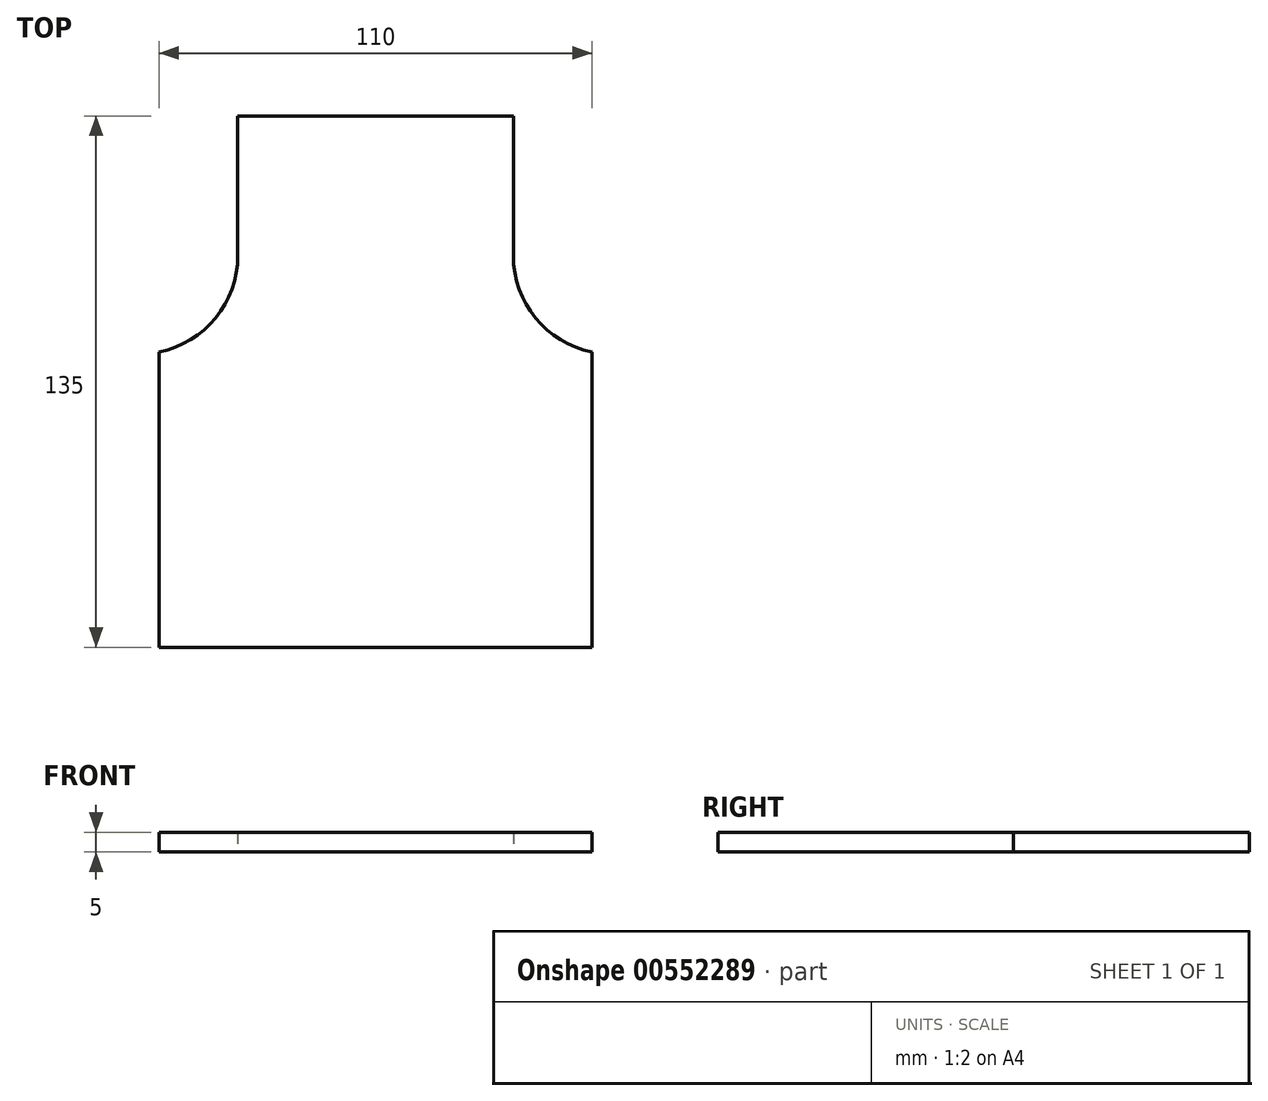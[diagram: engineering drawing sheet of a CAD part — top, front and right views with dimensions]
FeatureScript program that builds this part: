
annotation { "Feature Type Name" : "Feature", "Feature Type Description" : "" }
export const myFeature = defineFeature(function(context is Context, id is Id, definition is map)
    precondition{}
    {
        {
            var Q0;
            Q0=qCreatedBy(makeId("Top.planeOp"),FACE);
            var sketch = newSketch(context, id + "F0", { "sketchPlane" : qUnion([Q0])});
            skLineSegment(sketch, "E0", {"start": v(-35, 135) * mm, "end": v(-35, 75) * mm});
            skLineSegment(sketch, "E1", {"start": v(-35, 75) * mm, "end": v(-55, 75) * mm});
            skLineSegment(sketch, "E2", {"start": v(-55, 75) * mm, "end": v(-55, 0) * mm});
            skLineSegment(sketch, "E3", {"start": v(-55, 0) * mm, "end": v(55, 0) * mm});
            skLineSegment(sketch, "E4", {"start": v(55, 0) * mm, "end": v(55, 75) * mm});
            skLineSegment(sketch, "E5", {"start": v(55, 75) * mm, "end": v(35, 75) * mm});
            skLineSegment(sketch, "E6", {"start": v(35, 75) * mm, "end": v(35, 135) * mm});
            skLineSegment(sketch, "E7", {"start": v(35, 135) * mm, "end": v(-35, 135) * mm});
            skLineSegment(sketch, "E8", {"start": v(0, 135) * mm, "end": v(0, 0) * mm, "construction": true});
            skSolve(sketch);
        }
        {
            var Q0;
            Q0 = qSketchRegion(id + "F0", true);
            extrude(context, id + "F1", {"entities" : qUnion([Q0]), "depth" : 5 * mm, "offsetDistance" : 25.4 * mm});
        }
        {
            var Q0;
            Q0=makeQuery(id+"F1.opExtrude","SWEPT_EDGE",EDGE,{"disambiguationData":[OSD([sQuery(id+"F0.wireOp",EDGE,"E0"),sQuery(id+"F0.wireOp",EDGE,"E1")])]});
            var Q1;
            Q1=makeQuery(id+"F1.opExtrude","SWEPT_EDGE",EDGE,{"disambiguationData":[OSD([sQuery(id+"F0.wireOp",EDGE,"E5"),sQuery(id+"F0.wireOp",EDGE,"E6")])]});
            fillet(context, id + "F2", {"entities" : qUnion([Q0, Q1]), "radius" : 25 * mm, "tangentPropagation" : true, "allowEdgeOverflow" : false});
        }
    });
